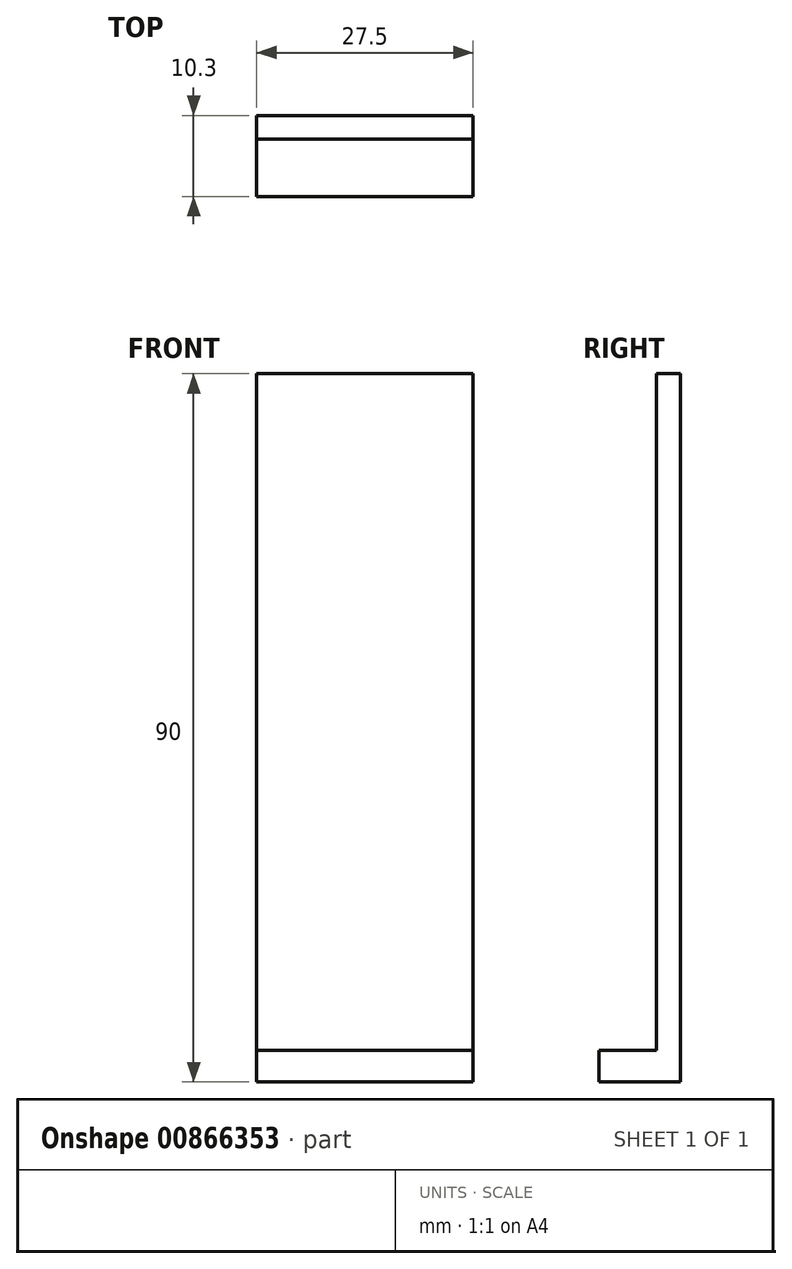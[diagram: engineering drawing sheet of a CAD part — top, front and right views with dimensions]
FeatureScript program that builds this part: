
annotation { "Feature Type Name" : "Feature", "Feature Type Description" : "" }
export const myFeature = defineFeature(function(context is Context, id is Id, definition is map)
    precondition{}
    {
        {
            var Q0;
            Q0=qCreatedBy(makeId("Front.planeOp"),FACE);
            var sketch = newSketch(context, id + "F0", { "sketchPlane" : qUnion([Q0])});
            skLineSegment(sketch, "E0.bottom", {"start": v(-13.75, 40) * mm, "end": v(13.75, 40) * mm});
            skLineSegment(sketch, "E0.top", {"start": v(-13.75, -50) * mm, "end": v(13.75, -50) * mm});
            skLineSegment(sketch, "E0.left", {"start": v(-13.75, 40) * mm, "end": v(-13.75, -50) * mm});
            skLineSegment(sketch, "E0.right", {"start": v(13.75, 40) * mm, "end": v(13.75, -50) * mm});
            skPoint(sketch, "E1", {"position": v(-13.75, 0) * mm});
            skPoint(sketch, "E2", {"position": v(0, 40) * mm});
            skSolve(sketch);
        }
        {
            var Q0;
            Q0=qSketchRegion(id+"F0",true);
            extrude(context, id + "F1", {"entities" : qUnion([Q0]), "depth" : 3 * mm, "offsetDistance" : 25.4 * mm});
        }
        {
            var Q0;
            Q0=makeQuery(id+"F1.opExtrude","SWEPT_FACE",FACE,{"disambiguationData":[OSD([sQuery(id+"F0.wireOp",EDGE,"E0.top")])]});
            var sketch = newSketch(context, id + "F2", { "sketchPlane" : qUnion([Q0])});
            skLineSegment(sketch, "E3.bottom", {"start": v(-13.75, 0) * mm, "end": v(13.75, 0) * mm});
            skLineSegment(sketch, "E3.top", {"start": v(-13.75, 10.3) * mm, "end": v(13.75, 10.3) * mm});
            skLineSegment(sketch, "E3.left", {"start": v(-13.75, 0) * mm, "end": v(-13.75, 10.3) * mm});
            skLineSegment(sketch, "E3.right", {"start": v(13.75, 0) * mm, "end": v(13.75, 10.3) * mm});
            skSolve(sketch);
        }
        {
            var Q0;
            Q0=qSketchRegion(id+"F2",true);
            extrude(context, id + "F3", {"entities" : qUnion([Q0]), "operationType" : NewBodyOperationType.ADD, "oppositeDirection" : true, "depth" : 4 * mm, "offsetDistance" : 25.4 * mm});
        }
    });
